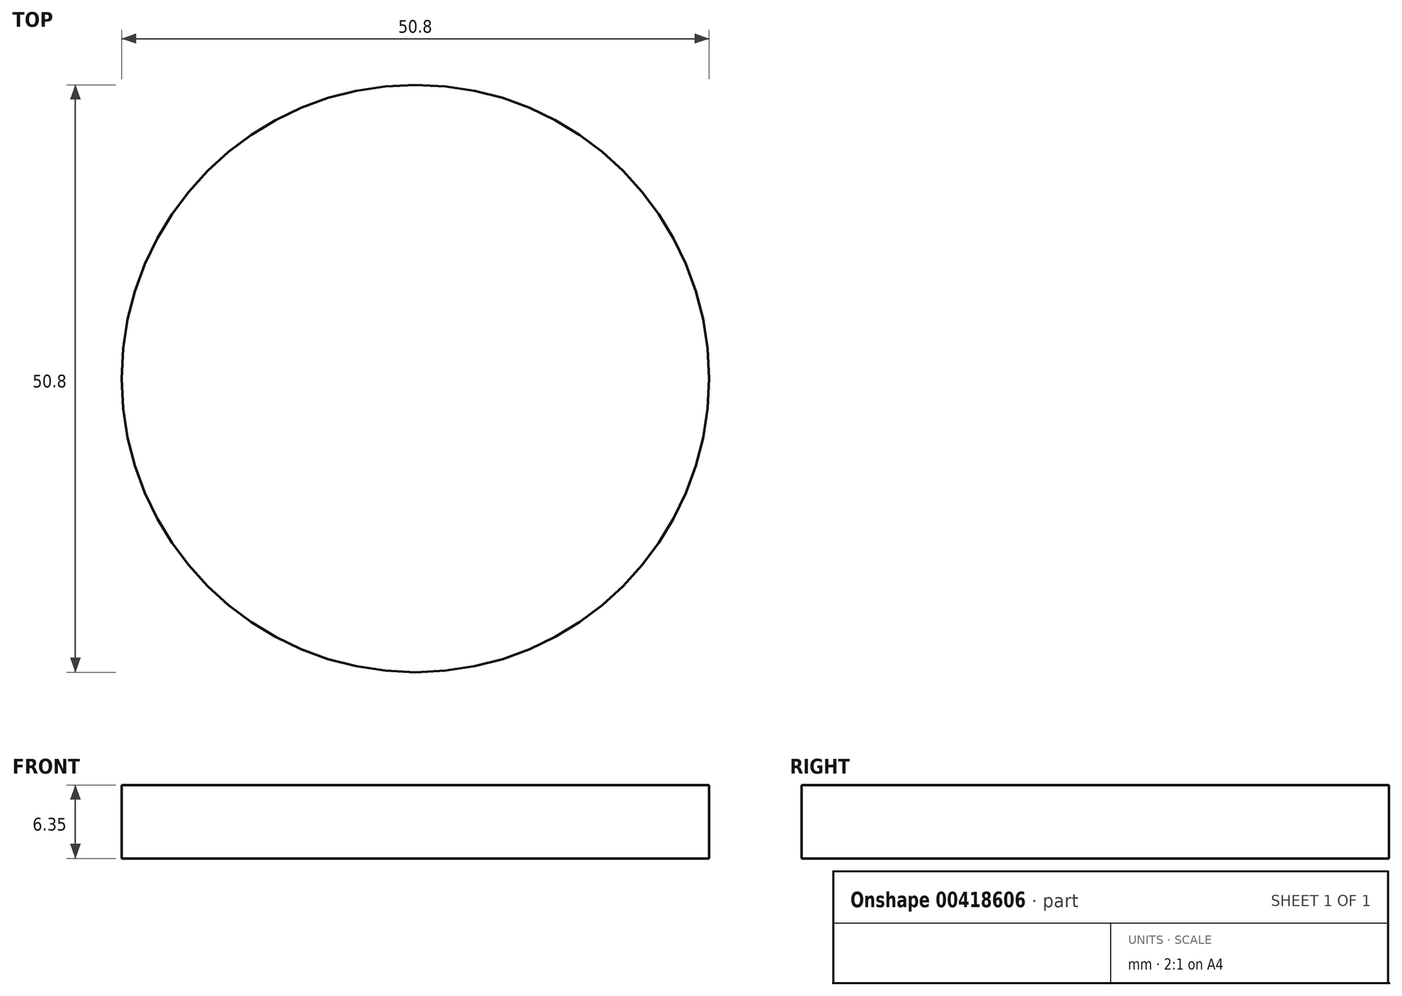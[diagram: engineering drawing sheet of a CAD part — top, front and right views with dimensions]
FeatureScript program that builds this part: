
annotation { "Feature Type Name" : "Feature", "Feature Type Description" : "" }
export const myFeature = defineFeature(function(context is Context, id is Id, definition is map)
    precondition{}
    {
        {
            var Q0;
            Q0=qCreatedBy(makeId("Top.planeOp"),FACE);
            var sketch = newSketch(context, id + "F0", { "sketchPlane" : qUnion([Q0])});
            skCircle(sketch, "E0", {"center": v(0, 0) * mm, "radius": 25.4 * mm});
            skSolve(sketch);
        }
        {
            var Q0;
            Q0=makeQuery(id+"F0.imprint","IMPRINT",FACE,{"disambiguationData":[TD([[makeQuery(id+"F0.imprint","IMPRINT",EDGE,{"derivedFrom":sQuery(id+"F0.wireOp",EDGE,"E0")}),1.0]])]});
            extrude(context, id + "F1", {"entities" : qUnion([Q0]), "depth" : 6.35 * mm});
        }
    });
